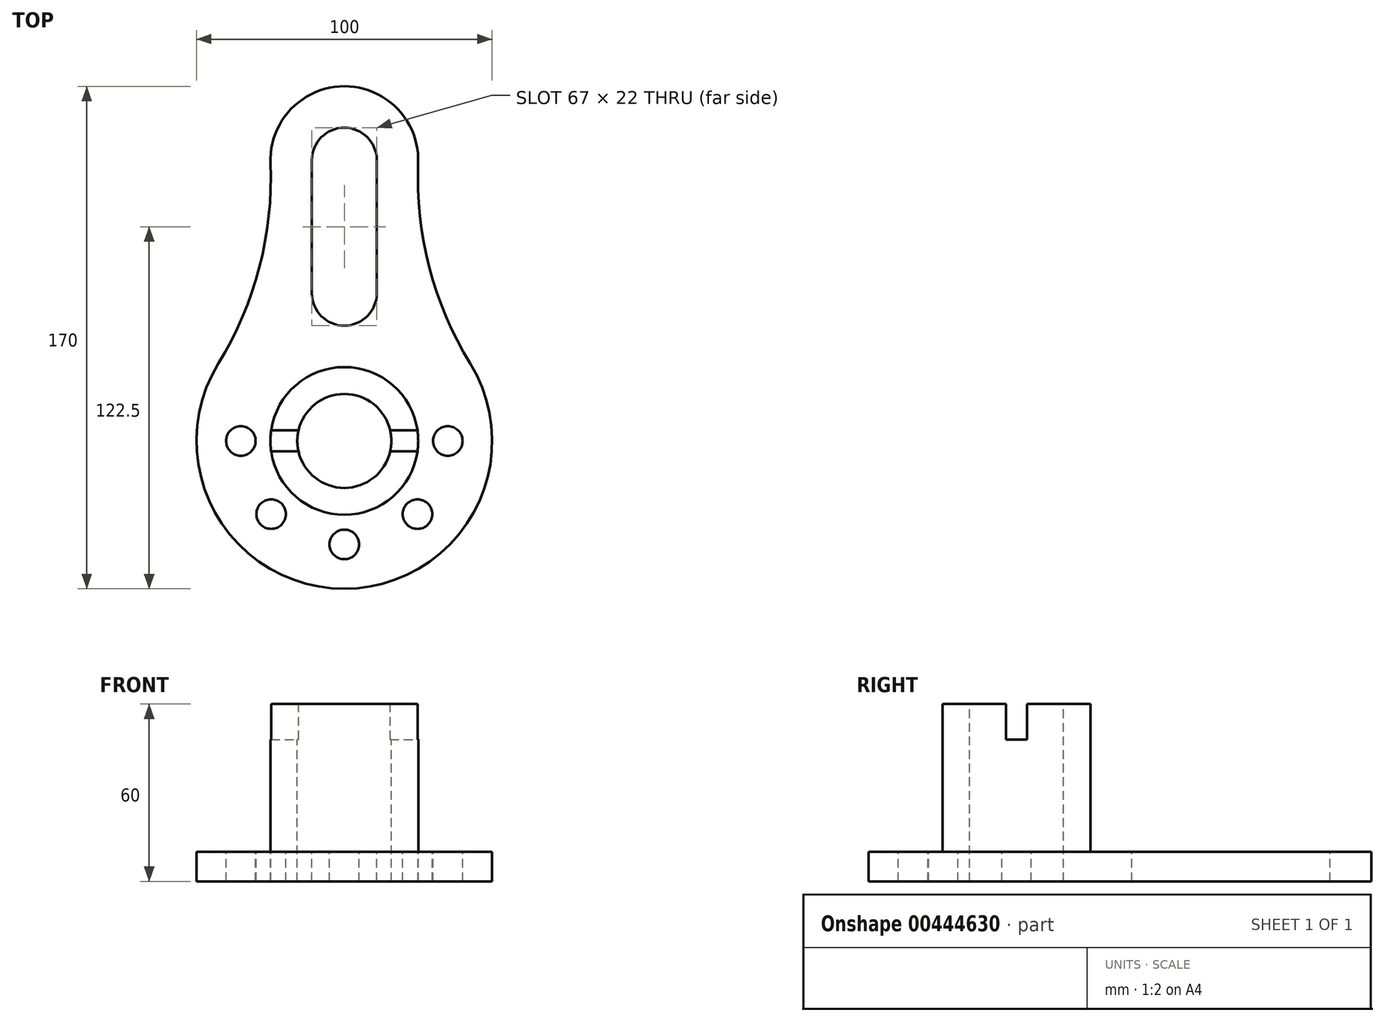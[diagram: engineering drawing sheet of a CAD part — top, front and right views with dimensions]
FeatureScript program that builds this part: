
annotation { "Feature Type Name" : "Feature", "Feature Type Description" : "" }
export const myFeature = defineFeature(function(context is Context, id is Id, definition is map)
    precondition{}
    {
        {
            var Q0;
            Q0=qCreatedBy(makeId("Top.planeOp"),FACE);
            var sketch = newSketch(context, id + "F0", { "sketchPlane" : qUnion([Q0])});
            skArc(sketch, "E0", {"start": v(24.98, -1.04) * mm, "mid": v(0, 25) * mm, "end": v(-24.98, -1.04) * mm});
            skArc(sketch, "E1", {"start": v(-42.6, -68.84) * mm, "mid": v(0, -145) * mm, "end": v(42.6, -68.84) * mm});
            skArc(sketch, "E2", {"start": v(24.98, -1.04) * mm, "mid": v(28.74, -36.26) * mm, "end": v(42.6, -68.84) * mm});
            skArc(sketch, "E3", {"start": v(-42.6, -68.84) * mm, "mid": v(-28.74, -36.26) * mm, "end": v(-24.98, -1.04) * mm});
            skLineSegment(sketch, "E4", {"start": v(0, -95) * mm, "end": v(0, 0) * mm, "construction": true});
            skCircle(sketch, "E5", {"center": v(0, -95) * mm, "radius": 15.9 * mm});
            skSolve(sketch);
        }
        {
            var Q0;
            Q0=makeQuery(id+"F0.imprint","IMPRINT",FACE,{"disambiguationData":[TD([[makeQuery(id+"F0.imprint","IMPRINT",EDGE,{"derivedFrom":sQuery(id+"F0.wireOp",EDGE,"E0")}),1.0]])]});
            extrude(context, id + "F1", {"entities" : qUnion([Q0]), "oppositeDirection" : true, "depth" : 10 * mm});
        }
        {
            var Q0;
            Q0=qCreatedBy(makeId("Top.planeOp"),FACE);
            var sketch = newSketch(context, id + "F2", { "sketchPlane" : qUnion([Q0])});
            skArc(sketch, "E6", {"start": v(-11, -45) * mm, "mid": v(0, -56) * mm, "end": v(11, -45) * mm});
            skArc(sketch, "E7", {"start": v(11, 0) * mm, "mid": v(0, 11) * mm, "end": v(-11, 0) * mm});
            skLineSegment(sketch, "E8", {"start": v(-11, -45) * mm, "end": v(-11, 0) * mm});
            skLineSegment(sketch, "E9", {"start": v(11, -45) * mm, "end": v(11, 0) * mm});
            skSolve(sketch);
        }
        {
            var Q0;
            Q0=makeQuery(id+"F2.imprint","IMPRINT",FACE,{"disambiguationData":[TD([[makeQuery(id+"F2.imprint","IMPRINT",EDGE,{"derivedFrom":sQuery(id+"F2.wireOp",EDGE,"E6")}),1.0]])]});
            extrude(context, id + "F3", {"entities" : qUnion([Q0]), "operationType" : NewBodyOperationType.REMOVE, "endBound" : BoundingType.UP_TO_NEXT, "oppositeDirection" : true, "depth" : 25 * mm});
        }
        {
            var Q0;
            Q0=makeQuery(id+"F1.opExtrude","CAP_FACE",FACE,{"disambiguationData":[OSD([sQuery(id+"F0.wireOp",EDGE,"E0"),sQuery(id+"F0.wireOp",EDGE,"E1"),sQuery(id+"F0.wireOp",EDGE,"E2"),sQuery(id+"F0.wireOp",EDGE,"E3")])],"isStart":true});
            var sketch = newSketch(context, id + "F4", { "sketchPlane" : qUnion([Q0])});
            skCircle(sketch, "E10", {"center": v(0, -95) * mm, "radius": 35 * mm, "construction": true});
            skCircle(sketch, "E11", {"center": v(-35, -95) * mm, "radius": 5 * mm});
            skCircle(sketch, "E12.1.0", {"center": v(-24.75, -119.75) * mm, "radius": 5 * mm});
            skCircle(sketch, "E12.2.0", {"center": v(0, -130) * mm, "radius": 5 * mm});
            skCircle(sketch, "E12.3.0", {"center": v(24.75, -119.75) * mm, "radius": 5 * mm});
            skCircle(sketch, "E12.4.0", {"center": v(35, -95) * mm, "radius": 5 * mm});
            skLineSegment(sketch, "E12.anchor1", {"start": v(0, -95) * mm, "end": v(-35, -95) * mm, "construction": true});
            skLineSegment(sketch, "E12.anchor2", {"start": v(0, -95) * mm, "end": v(35, -95) * mm, "construction": true});
            skSolve(sketch);
        }
        {
            var Q0;
            Q0 = qSketchRegion(id + "F4", true);
            extrude(context, id + "F5", {"entities" : qUnion([Q0]), "operationType" : NewBodyOperationType.REMOVE, "endBound" : BoundingType.UP_TO_NEXT, "oppositeDirection" : true, "depth" : 25 * mm});
        }
        {
            var Q0;
            Q0=makeQuery(id+"F1.opExtrude","CAP_FACE",FACE,{"disambiguationData":[OSD([sQuery(id+"F0.wireOp",EDGE,"E0"),sQuery(id+"F0.wireOp",EDGE,"E1"),sQuery(id+"F0.wireOp",EDGE,"E2"),sQuery(id+"F0.wireOp",EDGE,"E3"),sQuery(id+"F0.wireOp",EDGE,"E5")])],"isStart":true});
            var sketch = newSketch(context, id + "F6", { "sketchPlane" : qUnion([Q0])});
            skCircle(sketch, "E13", {"center": v(0, -95) * mm, "radius": 25 * mm});
            skCircle(sketch, "E14.0", {"center": v(0, -95) * mm, "radius": 15.9 * mm});
            skSolve(sketch);
        }
        {
            var Q0;
            Q0 = qSketchRegion(id + "F6", true);
            extrude(context, id + "F7", {"entities" : qUnion([Q0]), "operationType" : NewBodyOperationType.ADD, "depth" : 50 * mm});
        }
        {
            var Q0;
            Q0=qCreatedBy(makeId("Right.planeOp"),FACE);
            var sketch = newSketch(context, id + "F8", { "sketchPlane" : qUnion([Q0])});
            skLineSegment(sketch, "E15.bottom", {"start": v(-98.55, 50) * mm, "end": v(-91.45, 50) * mm});
            skLineSegment(sketch, "E15.top", {"start": v(-98.55, 38) * mm, "end": v(-91.45, 38) * mm});
            skLineSegment(sketch, "E15.left", {"start": v(-98.55, 50) * mm, "end": v(-98.55, 38) * mm});
            skLineSegment(sketch, "E15.right", {"start": v(-91.45, 50) * mm, "end": v(-91.45, 38) * mm});
            skLineSegment(sketch, "E16", {"start": v(-95, 50) * mm, "end": v(-95, 38) * mm, "construction": true});
            skSolve(sketch);
        }
        {
            var Q0;
            Q0 = qSketchRegion(id + "F8", true);
            extrude(context, id + "F9", {"entities" : qUnion([Q0]), "operationType" : NewBodyOperationType.REMOVE, "oppositeDirection" : true, "depth" : 50 * mm, "symmetric" : true});
        }
    });
